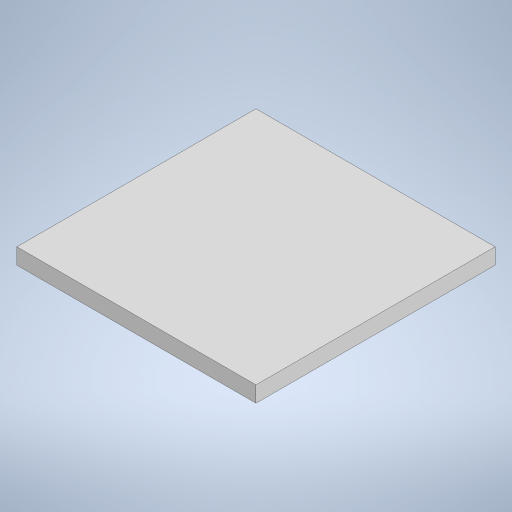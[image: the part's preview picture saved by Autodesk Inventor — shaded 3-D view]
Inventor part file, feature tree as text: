
AUTODESK INVENTOR PART (.ipt)
format: ipt  version: 2023 (Build 270158000, 158)  size: 231,424 bytes
history: native  units: mm
features: extrude x1, sketch x1
ambient origin geometry x8: Origin, YZ Plane, XZ Plane, XY Plane, X Axis, Y Axis, Z Axis, Center Point
bodies: Solid1 (feature_tree)
feature tree (2):
  extrude  "Extrusion1"  Depth=30.0mm
  sketch  "Sketch1"  dims[d0=30.0mm d1=30.0mm d2=2.0mm d3=0.0mm]
